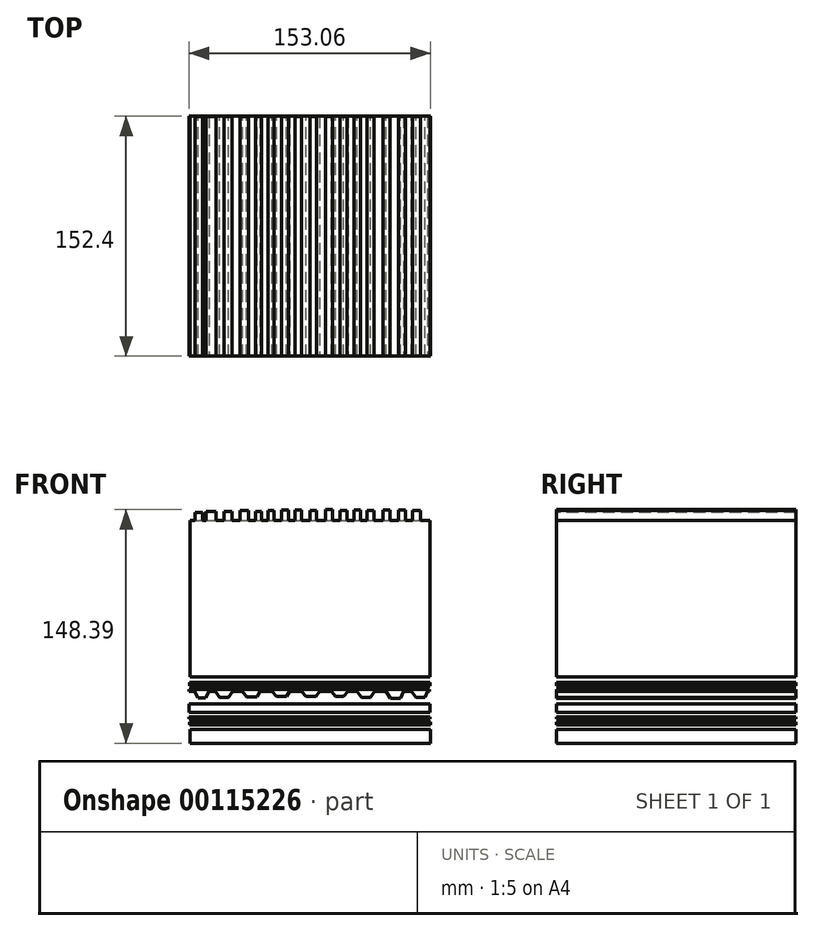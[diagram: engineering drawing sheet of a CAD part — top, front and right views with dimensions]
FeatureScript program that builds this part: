
annotation { "Feature Type Name" : "Feature", "Feature Type Description" : "" }
export const myFeature = defineFeature(function(context is Context, id is Id, definition is map)
    precondition{}
    {
        {
            var Q0;
            Q0=qCreatedBy(makeId("Front.planeOp"),FACE);
            var sketch = newSketch(context, id + "F0", { "sketchPlane" : qUnion([Q0])});
            skLineSegment(sketch, "E0.bottom", {"start": v(-76.06, -75.93) * mm, "end": v(76.41, -75.93) * mm});
            skLineSegment(sketch, "E0.top", {"start": v(-76.06, -67.24) * mm, "end": v(76.41, -67.24) * mm});
            skLineSegment(sketch, "E0.left", {"start": v(-76.06, -75.93) * mm, "end": v(-76.06, -67.24) * mm});
            skLineSegment(sketch, "E0.right", {"start": v(76.41, -75.93) * mm, "end": v(76.41, -67.24) * mm});
            skSolve(sketch);
        }
        {
            var Q0;
            Q0 = qSketchRegion(id + "F0", true);
            extrude(context, id + "F1", {"entities" : qUnion([Q0]), "depth" : 152.4 * mm});
        }
        {
            var Q0;
            Q0=qCreatedBy(makeId("Front.planeOp"),FACE);
            var sketch = newSketch(context, id + "F2", { "sketchPlane" : qUnion([Q0])});
            skLineSegment(sketch, "E1.bottom", {"start": v(-76.36, -64.25) * mm, "end": v(76.41, -64.25) * mm});
            skLineSegment(sketch, "E1.top", {"start": v(-76.36, -62.45) * mm, "end": v(76.41, -62.45) * mm});
            skLineSegment(sketch, "E1.left", {"start": v(-76.36, -64.25) * mm, "end": v(-76.36, -62.45) * mm});
            skLineSegment(sketch, "E1.right", {"start": v(76.41, -64.25) * mm, "end": v(76.41, -62.45) * mm});
            skSolve(sketch);
        }
        {
            var Q0;
            Q0 = qSketchRegion(id + "F2", true);
            extrude(context, id + "F3", {"entities" : qUnion([Q0]), "depth" : 152.4 * mm});
        }
        {
            var Q0;
            Q0=qCreatedBy(makeId("Front.planeOp"),FACE);
            var sketch = newSketch(context, id + "F4", { "sketchPlane" : qUnion([Q0])});
            skLineSegment(sketch, "E2.bottom", {"start": v(-76.65, -60.36) * mm, "end": v(76.11, -60.36) * mm});
            skLineSegment(sketch, "E2.top", {"start": v(-76.65, -59.16) * mm, "end": v(76.11, -59.16) * mm});
            skLineSegment(sketch, "E2.left", {"start": v(-76.65, -60.36) * mm, "end": v(-76.65, -59.16) * mm});
            skLineSegment(sketch, "E2.right", {"start": v(76.11, -60.36) * mm, "end": v(76.11, -59.16) * mm});
            skSolve(sketch);
        }
        {
            var Q0;
            Q0 = qSketchRegion(id + "F4", true);
            extrude(context, id + "F5", {"entities" : qUnion([Q0]), "depth" : 152.4 * mm});
        }
        {
            var Q0;
            Q0=qCreatedBy(makeId("Front.planeOp"),FACE);
            var sketch = newSketch(context, id + "F6", { "sketchPlane" : qUnion([Q0])});
            skLineSegment(sketch, "E3.bottom", {"start": v(-76.65, -56.46) * mm, "end": v(76.11, -56.46) * mm});
            skLineSegment(sketch, "E3.top", {"start": v(-76.65, -50.77) * mm, "end": v(76.11, -50.77) * mm});
            skLineSegment(sketch, "E3.left", {"start": v(-76.65, -56.46) * mm, "end": v(-76.65, -50.77) * mm});
            skLineSegment(sketch, "E3.right", {"start": v(76.11, -56.46) * mm, "end": v(76.11, -50.77) * mm});
            skSolve(sketch);
        }
        {
            var Q0;
            Q0 = qSketchRegion(id + "F6", true);
            extrude(context, id + "F7", {"entities" : qUnion([Q0]), "depth" : 152.4 * mm});
        }
        {
            var Q0;
            Q0=qCreatedBy(makeId("Front.planeOp"),FACE);
            var sketch = newSketch(context, id + "F8", { "sketchPlane" : qUnion([Q0])});
            skLineSegment(sketch, "E4.bottom", {"start": v(-76.65, -42.98) * mm, "end": v(75.81, -42.98) * mm});
            skLineSegment(sketch, "E4.top", {"start": v(-76.65, -41.78) * mm, "end": v(75.81, -41.78) * mm});
            skLineSegment(sketch, "E4.left", {"start": v(-76.65, -42.98) * mm, "end": v(-76.65, -41.78) * mm});
            skLineSegment(sketch, "E4.right", {"start": v(75.81, -42.98) * mm, "end": v(75.81, -41.78) * mm});
            skSolve(sketch);
        }
        {
            var Q0;
            Q0 = qSketchRegion(id + "F8", true);
            extrude(context, id + "F9", {"entities" : qUnion([Q0]), "depth" : 152.4 * mm});
        }
        {
            var Q0;
            Q0=qCreatedBy(makeId("Front.planeOp"),FACE);
            var sketch = newSketch(context, id + "F10", { "sketchPlane" : qUnion([Q0])});
            skLineSegment(sketch, "E5.bottom", {"start": v(-76.5, -39.35) * mm, "end": v(76.26, -39.35) * mm});
            skLineSegment(sketch, "E5.top", {"start": v(-76.5, -37.32) * mm, "end": v(76.26, -37.32) * mm});
            skLineSegment(sketch, "E5.left", {"start": v(-76.5, -39.35) * mm, "end": v(-76.5, -37.32) * mm});
            skLineSegment(sketch, "E5.right", {"start": v(76.26, -39.35) * mm, "end": v(76.26, -37.32) * mm});
            skSolve(sketch);
        }
        {
            var Q0;
            Q0 = qSketchRegion(id + "F10", true);
            extrude(context, id + "F11", {"entities" : qUnion([Q0]), "depth" : 152.4 * mm});
        }
        {
            var Q0;
            Q0=qCreatedBy(makeId("Front.planeOp"),FACE);
            var sketch = newSketch(context, id + "F12", { "sketchPlane" : qUnion([Q0])});
            skLineSegment(sketch, "E6.bottom", {"start": v(-76.21, -33.83) * mm, "end": v(76.26, -33.83) * mm});
            skLineSegment(sketch, "E6.top", {"start": v(-76.21, 65.49) * mm, "end": v(76.26, 65.49) * mm});
            skLineSegment(sketch, "E6.left", {"start": v(-76.21, -33.83) * mm, "end": v(-76.21, 65.49) * mm});
            skLineSegment(sketch, "E6.right", {"start": v(76.26, -33.83) * mm, "end": v(76.26, 65.49) * mm});
            skSolve(sketch);
        }
        {
            var Q0;
            Q0=makeQuery(id+"F12.imprint","IMPRINT",FACE,{"disambiguationData":[TD([[makeQuery(id+"F12.imprint","IMPRINT",EDGE,{"derivedFrom":sQuery(id+"F12.wireOp",EDGE,"E6.bottom")}),1.0]])]});
            extrude(context, id + "F13", {"entities" : qUnion([Q0]), "depth" : 152.4 * mm});
        }
        {
            var Q0;
            Q0=qCreatedBy(makeId("Front.planeOp"),FACE);
            var sketch = newSketch(context, id + "F14", { "sketchPlane" : qUnion([Q0])});
            skLineSegment(sketch, "E7", {"start": v(-70.98, -47.2) * mm, "end": v(-66.34, -47.2) * mm});
            skLineSegment(sketch, "E8", {"start": v(-66.34, -47.2) * mm, "end": v(-63.72, -42.55) * mm});
            skLineSegment(sketch, "E9", {"start": v(-70.98, -47.2) * mm, "end": v(-73.6, -42.55) * mm});
            skLineSegment(sketch, "E10", {"start": v(-73.6, -42.55) * mm, "end": v(-63.72, -42.55) * mm});
            skSolve(sketch);
        }
        {
            var Q0;
            Q0 = qSketchRegion(id + "F14", true);
            extrude(context, id + "F15", {"entities" : qUnion([Q0]), "operationType" : NewBodyOperationType.ADD, "depth" : 152.4 * mm});
        }
        {
            var Q0;
            Q0=qCreatedBy(makeId("Front.planeOp"),FACE);
            var sketch = newSketch(context, id + "F16", { "sketchPlane" : qUnion([Q0])});
            skLineSegment(sketch, "E11", {"start": v(-60.24, -42.55) * mm, "end": v(-57.33, -46.9) * mm});
            skLineSegment(sketch, "E12", {"start": v(-57.33, -46.9) * mm, "end": v(-51.82, -46.9) * mm});
            skLineSegment(sketch, "E13", {"start": v(-51.82, -46.9) * mm, "end": v(-49.2, -42.84) * mm});
            skLineSegment(sketch, "E14", {"start": v(-49.2, -42.84) * mm, "end": v(-42.81, -42.84) * mm});
            skLineSegment(sketch, "E15", {"start": v(-42.81, -42.84) * mm, "end": v(-40.2, -46.32) * mm});
            skLineSegment(sketch, "E16", {"start": v(-40.2, -46.32) * mm, "end": v(-33.52, -46.32) * mm});
            skLineSegment(sketch, "E17", {"start": v(-33.52, -46.32) * mm, "end": v(-31.49, -42.26) * mm});
            skLineSegment(sketch, "E18", {"start": v(-31.49, -42.26) * mm, "end": v(-24.8, -42.26) * mm});
            skLineSegment(sketch, "E19", {"start": v(-24.8, -42.26) * mm, "end": v(-21.32, -46.03) * mm});
            skLineSegment(sketch, "E20", {"start": v(-21.32, -46.03) * mm, "end": v(-14.93, -46.03) * mm});
            skLineSegment(sketch, "E21", {"start": v(-14.93, -46.03) * mm, "end": v(-12.6, -42.26) * mm});
            skLineSegment(sketch, "E22", {"start": v(-12.6, -42.26) * mm, "end": v(-5.93, -42.26) * mm});
            skLineSegment(sketch, "E23", {"start": v(-5.93, -42.26) * mm, "end": v(-2.45, -46.03) * mm});
            skLineSegment(sketch, "E24", {"start": v(-2.45, -46.03) * mm, "end": v(3.94, -46.03) * mm});
            skLineSegment(sketch, "E25", {"start": v(3.94, -46.03) * mm, "end": v(6.56, -42.55) * mm});
            skLineSegment(sketch, "E26", {"start": v(6.56, -42.55) * mm, "end": v(13.24, -42.55) * mm});
            skLineSegment(sketch, "E27", {"start": v(13.24, -42.55) * mm, "end": v(16.14, -46.03) * mm});
            skLineSegment(sketch, "E28", {"start": v(16.14, -46.03) * mm, "end": v(21.37, -46.03) * mm});
            skLineSegment(sketch, "E29", {"start": v(21.37, -46.03) * mm, "end": v(24.27, -42.84) * mm});
            skLineSegment(sketch, "E30", {"start": v(24.27, -42.84) * mm, "end": v(29.8, -42.84) * mm});
            skLineSegment(sketch, "E31", {"start": v(29.8, -42.84) * mm, "end": v(32.7, -46.9) * mm});
            skLineSegment(sketch, "E32", {"start": v(32.7, -46.9) * mm, "end": v(38.5, -46.9) * mm});
            skLineSegment(sketch, "E33", {"start": v(38.5, -46.9) * mm, "end": v(41.12, -42.55) * mm});
            skLineSegment(sketch, "E34", {"start": v(41.12, -42.55) * mm, "end": v(48.09, -42.55) * mm});
            skLineSegment(sketch, "E35", {"start": v(48.09, -42.55) * mm, "end": v(51.28, -47.48) * mm});
            skLineSegment(sketch, "E36", {"start": v(51.28, -47.48) * mm, "end": v(57.38, -47.48) * mm});
            skLineSegment(sketch, "E37", {"start": v(57.38, -47.48) * mm, "end": v(59.7, -42.55) * mm});
            skLineSegment(sketch, "E38", {"start": v(59.7, -42.55) * mm, "end": v(64.06, -42.55) * mm});
            skLineSegment(sketch, "E39", {"start": v(64.06, -42.55) * mm, "end": v(67.25, -46.9) * mm});
            skLineSegment(sketch, "E40", {"start": v(67.25, -46.9) * mm, "end": v(73.06, -46.9) * mm});
            skLineSegment(sketch, "E41", {"start": v(73.06, -46.9) * mm, "end": v(75.1, -42.26) * mm});
            skLineSegment(sketch, "E42", {"start": v(75.1, -42.26) * mm, "end": v(-60.24, -42.55) * mm});
            skSolve(sketch);
        }
        {
            var Q0;
            Q0 = qSketchRegion(id + "F16", true);
            extrude(context, id + "F17", {"entities" : qUnion([Q0]), "operationType" : NewBodyOperationType.ADD, "depth" : 152.4 * mm});
        }
        {
            var Q0;
            Q0=makeQuery(id+"F13.opExtrude","CAP_FACE",FACE,{"disambiguationData":[OSD([sQuery(id+"F12.wireOp",EDGE,"E6.bottom"),sQuery(id+"F12.wireOp",EDGE,"E6.top"),sQuery(id+"F12.wireOp",EDGE,"E6.left"),sQuery(id+"F12.wireOp",EDGE,"E6.right")])],"isStart":false});
            var sketch = newSketch(context, id + "F18", { "sketchPlane" : qUnion([Q0])});
            skLineSegment(sketch, "E43", {"start": v(-73.02, 65.49) * mm, "end": v(-73.02, 70.72) * mm});
            skLineSegment(sketch, "E44", {"start": v(-73.02, 70.72) * mm, "end": v(-68.37, 70.72) * mm});
            skLineSegment(sketch, "E45", {"start": v(-68.37, 70.72) * mm, "end": v(-68.37, 65.49) * mm});
            skLineSegment(sketch, "E46", {"start": v(-68.45, 65.5) * mm, "end": v(-68.4, 65.49) * mm});
            skLineSegment(sketch, "E47", {"start": v(-65.86, 65.49) * mm, "end": v(-65.86, 71.4) * mm});
            skLineSegment(sketch, "E48", {"start": v(-66.24, 71.4) * mm, "end": v(-59.66, 71.4) * mm});
            skLineSegment(sketch, "E49", {"start": v(-59.66, 71.4) * mm, "end": v(-59.66, 65.49) * mm});
            skLineSegment(sketch, "E50", {"start": v(-54.65, 65.49) * mm, "end": v(-49.42, 65.49) * mm});
            skLineSegment(sketch, "E51", {"start": v(-49.42, 65.49) * mm, "end": v(-49.42, 71.4) * mm});
            skLineSegment(sketch, "E52", {"start": v(-54.65, 71.4) * mm, "end": v(-49.42, 71.4) * mm});
            skLineSegment(sketch, "E53", {"start": v(-54.65, 71.4) * mm, "end": v(-54.65, 65.49) * mm});
            skLineSegment(sketch, "E54", {"start": v(-44.27, 65.49) * mm, "end": v(-44.27, 71.88) * mm});
            skLineSegment(sketch, "E55", {"start": v(-44.27, 71.88) * mm, "end": v(-39.04, 71.88) * mm});
            skLineSegment(sketch, "E56", {"start": v(-39.04, 71.88) * mm, "end": v(-39.04, 65.49) * mm});
            skLineSegment(sketch, "E57", {"start": v(-39.04, 65.49) * mm, "end": v(-34.68, 65.49) * mm});
            skLineSegment(sketch, "E58", {"start": v(-34.68, 65.49) * mm, "end": v(-34.68, 71.3) * mm});
            skLineSegment(sketch, "E59", {"start": v(-34.68, 71.3) * mm, "end": v(-30.62, 71.3) * mm});
            skLineSegment(sketch, "E60", {"start": v(-30.62, 71.3) * mm, "end": v(-30.62, 65.49) * mm});
            skLineSegment(sketch, "E61", {"start": v(-30.62, 65.49) * mm, "end": v(-26.55, 65.49) * mm});
            skLineSegment(sketch, "E62", {"start": v(-26.55, 65.49) * mm, "end": v(-26.55, 71.88) * mm});
            skLineSegment(sketch, "E63", {"start": v(-26.55, 71.88) * mm, "end": v(-22.77, 71.88) * mm});
            skLineSegment(sketch, "E64", {"start": v(-22.77, 71.88) * mm, "end": v(-22.77, 65.49) * mm});
            skLineSegment(sketch, "E65", {"start": v(-22.77, 65.49) * mm, "end": v(-18.13, 65.49) * mm});
            skLineSegment(sketch, "E66", {"start": v(-18.13, 65.49) * mm, "end": v(-18.13, 72.17) * mm});
            skLineSegment(sketch, "E67", {"start": v(-18.13, 72.17) * mm, "end": v(-13.48, 72.17) * mm});
            skLineSegment(sketch, "E68", {"start": v(-13.48, 72.17) * mm, "end": v(-13.48, 65.49) * mm});
            skLineSegment(sketch, "E69", {"start": v(-13.48, 65.49) * mm, "end": v(-9.42, 65.49) * mm});
            skLineSegment(sketch, "E70", {"start": v(-9.42, 65.49) * mm, "end": v(-9.42, 72.17) * mm});
            skLineSegment(sketch, "E71", {"start": v(-9.42, 72.17) * mm, "end": v(-5.35, 72.17) * mm});
            skLineSegment(sketch, "E72", {"start": v(-5.35, 72.17) * mm, "end": v(-5.35, 65.49) * mm});
            skLineSegment(sketch, "E73", {"start": v(-5.35, 65.49) * mm, "end": v(0.02, 65.49) * mm});
            skLineSegment(sketch, "E74", {"start": v(0.02, 65.49) * mm, "end": v(0.02, 71.88) * mm});
            skLineSegment(sketch, "E75", {"start": v(0.02, 71.88) * mm, "end": v(4.23, 71.88) * mm});
            skLineSegment(sketch, "E76", {"start": v(4.23, 71.88) * mm, "end": v(4.23, 65.49) * mm});
            skLineSegment(sketch, "E77", {"start": v(4.23, 65.49) * mm, "end": v(9.75, 65.49) * mm});
            skLineSegment(sketch, "E78", {"start": v(9.75, 65.49) * mm, "end": v(9.75, 72.46) * mm});
            skLineSegment(sketch, "E79", {"start": v(9.75, 72.46) * mm, "end": v(14.4, 72.46) * mm});
            skLineSegment(sketch, "E80", {"start": v(14.4, 72.46) * mm, "end": v(14.4, 65.49) * mm});
            skLineSegment(sketch, "E81", {"start": v(14.4, 65.49) * mm, "end": v(19.05, 65.49) * mm});
            skLineSegment(sketch, "E82", {"start": v(19.05, 65.49) * mm, "end": v(19.05, 71.88) * mm});
            skLineSegment(sketch, "E83", {"start": v(19.05, 71.88) * mm, "end": v(23.4, 71.88) * mm});
            skLineSegment(sketch, "E84", {"start": v(23.4, 71.88) * mm, "end": v(23.4, 65.49) * mm});
            skLineSegment(sketch, "E85", {"start": v(23.4, 65.49) * mm, "end": v(28.05, 65.49) * mm});
            skLineSegment(sketch, "E86", {"start": v(28.05, 65.49) * mm, "end": v(28.05, 72.17) * mm});
            skLineSegment(sketch, "E87", {"start": v(28.05, 72.17) * mm, "end": v(32.11, 72.17) * mm});
            skLineSegment(sketch, "E88", {"start": v(32.11, 72.17) * mm, "end": v(32.11, 65.49) * mm});
            skLineSegment(sketch, "E89", {"start": v(36.18, 65.49) * mm, "end": v(36.18, 71.88) * mm});
            skLineSegment(sketch, "E90", {"start": v(36.18, 71.88) * mm, "end": v(40.83, 71.88) * mm});
            skLineSegment(sketch, "E91", {"start": v(40.83, 72.17) * mm, "end": v(40.83, 65.49) * mm});
            skLineSegment(sketch, "E92", {"start": v(40.83, 65.49) * mm, "end": v(46.34, 65.49) * mm});
            skLineSegment(sketch, "E93", {"start": v(46.34, 65.49) * mm, "end": v(46.34, 72.17) * mm});
            skLineSegment(sketch, "E94", {"start": v(46.34, 72.17) * mm, "end": v(51, 72.17) * mm});
            skLineSegment(sketch, "E95", {"start": v(51, 72.17) * mm, "end": v(51, 65.49) * mm});
            skLineSegment(sketch, "E96", {"start": v(51, 65.49) * mm, "end": v(56.22, 65.49) * mm});
            skLineSegment(sketch, "E97", {"start": v(56.22, 65.49) * mm, "end": v(56.22, 72.17) * mm});
            skLineSegment(sketch, "E98", {"start": v(56.22, 72.17) * mm, "end": v(60.58, 72.17) * mm});
            skLineSegment(sketch, "E99", {"start": v(60.58, 72.17) * mm, "end": v(60.58, 65.49) * mm});
            skLineSegment(sketch, "E100", {"start": v(60.58, 65.49) * mm, "end": v(65.22, 65.49) * mm});
            skLineSegment(sketch, "E101", {"start": v(65.22, 65.49) * mm, "end": v(65.22, 71.88) * mm});
            skLineSegment(sketch, "E102", {"start": v(65.22, 71.88) * mm, "end": v(70.16, 71.88) * mm});
            skLineSegment(sketch, "E103", {"start": v(70.16, 71.88) * mm, "end": v(70.16, 65.49) * mm});
            skLineSegment(sketch, "E104", {"start": v(-73.02, 65.49) * mm, "end": v(70.16, 65.49) * mm});
            skSolve(sketch);
        }
        {
            var Q0;
            Q0 = qSketchRegion(id + "F18", true);
            extrude(context, id + "F19", {"entities" : qUnion([Q0]), "operationType" : NewBodyOperationType.ADD, "oppositeDirection" : true, "depth" : 152.15 * mm});
        }
    });
